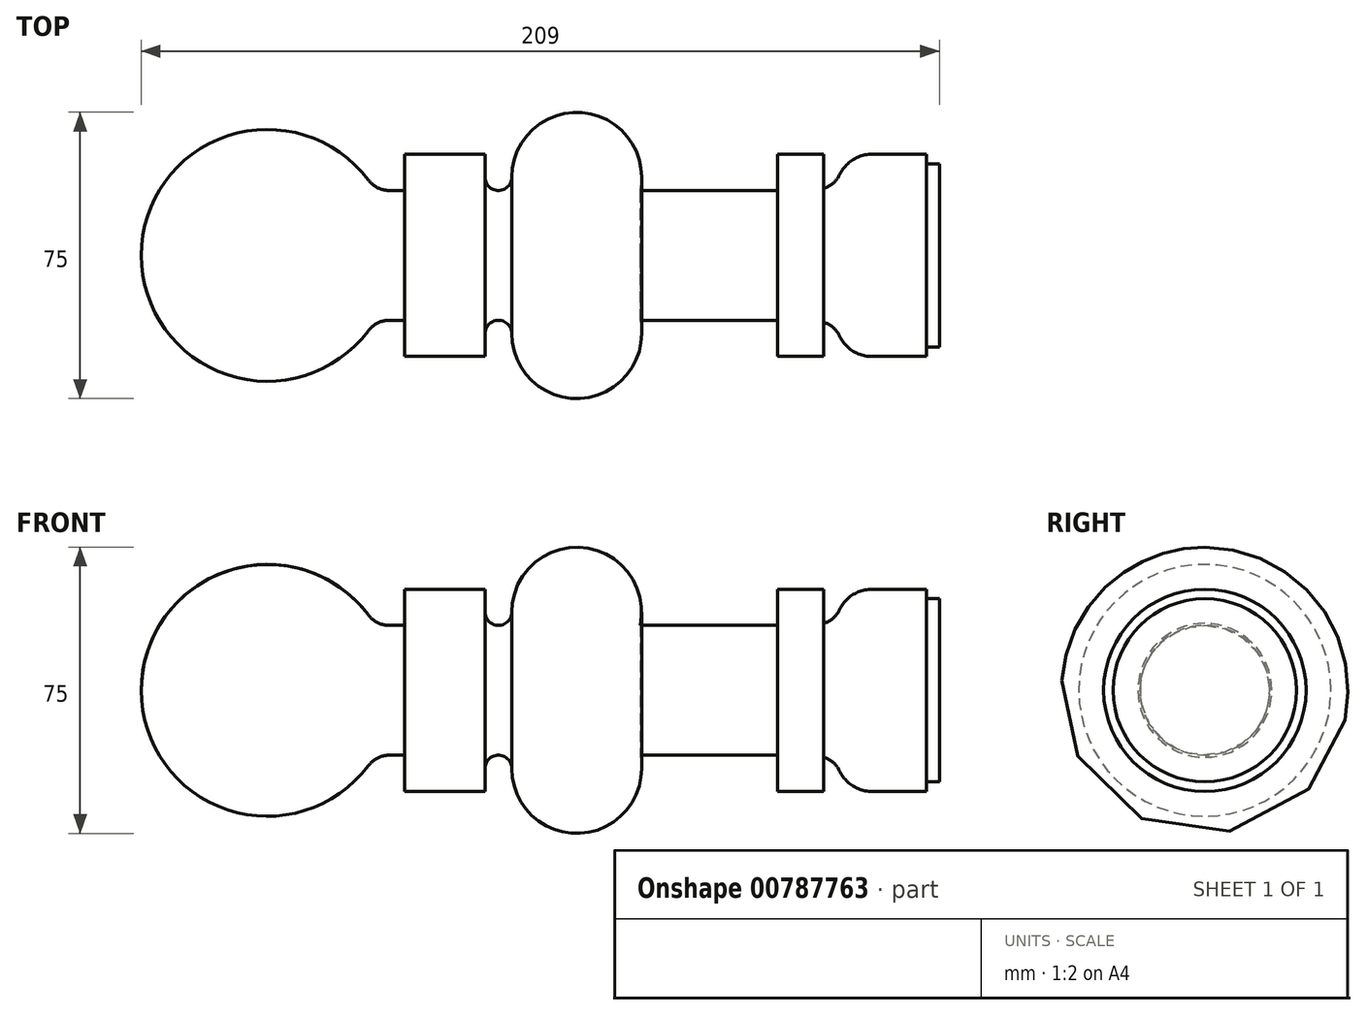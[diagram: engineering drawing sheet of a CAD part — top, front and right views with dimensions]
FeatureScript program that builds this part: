
annotation { "Feature Type Name" : "Feature", "Feature Type Description" : "" }
export const myFeature = defineFeature(function(context is Context, id is Id, definition is map)
    precondition{}
    {
        {
            var Q0;
            Q0=qCreatedBy(makeId("Front.planeOp"),FACE);
            var sketch = newSketch(context, id + "F0", { "sketchPlane" : qUnion([Q0])});
            skLineSegment(sketch, "E0", {"start": v(0, 0) * mm, "end": v(176, 0) * mm});
            skArc(sketch, "E1", {"start": v(26.4, 19.8) * mm, "mid": v(-10.44, 31.3) * mm, "end": v(-33, 0) * mm});
            skLineSegment(sketch, "E2", {"start": v(0, 0) * mm, "end": v(-33, 0) * mm});
            skLineSegment(sketch, "E3", {"start": v(36, 17) * mm, "end": v(36, 26.5) * mm});
            skLineSegment(sketch, "E4", {"start": v(36, 26.5) * mm, "end": v(57, 26.5) * mm});
            skLineSegment(sketch, "E5", {"start": v(57, 26.5) * mm, "end": v(57, 20.5) * mm});
            skLineSegment(sketch, "E6", {"start": v(36, 17) * mm, "end": v(32, 17) * mm});
            skArc(sketch, "E7.filletArc", {"start": v(26.4, 19.8) * mm, "mid": v(28.87, 17.74) * mm, "end": v(32, 17) * mm});
            skArc(sketch, "E8", {"start": v(57, 20.5) * mm, "mid": v(60.5, 17) * mm, "end": v(64, 20.5) * mm});
            skArc(sketch, "E9", {"start": v(97.64, 17) * mm, "mid": v(82.76, 37.4) * mm, "end": v(64, 20.5) * mm});
            skLineSegment(sketch, "E10", {"start": v(97.64, 17) * mm, "end": v(133.64, 17) * mm});
            skLineSegment(sketch, "E11", {"start": v(133.64, 17) * mm, "end": v(133.64, 26.5) * mm});
            skLineSegment(sketch, "E12", {"start": v(133.64, 26.5) * mm, "end": v(145.64, 26.5) * mm});
            skLineSegment(sketch, "E13", {"start": v(145.64, 26.5) * mm, "end": v(145.64, 17.54) * mm});
            skLineSegment(sketch, "E14", {"start": v(172.64, 24) * mm, "end": v(172.64, 26.5) * mm});
            skLineSegment(sketch, "E15", {"start": v(172.64, 26.5) * mm, "end": v(158.38, 26.5) * mm});
            skArc(sketch, "E16", {"start": v(158.38, 26.5) * mm, "mid": v(153.29, 25.02) * mm, "end": v(149.78, 21.04) * mm});
            skArc(sketch, "E17", {"start": v(145.64, 17.54) * mm, "mid": v(148.1, 18.84) * mm, "end": v(149.78, 21.04) * mm});
            skLineSegment(sketch, "E18", {"start": v(176, 0) * mm, "end": v(176, 24) * mm});
            skLineSegment(sketch, "E19", {"start": v(176, 24) * mm, "end": v(172.64, 24) * mm});
            skPoint(sketch, "E20.orphan", {"position": v(145.64, 0) * mm});
            skSolve(sketch);
        }
        {
            var Q0;
            Q0=makeQuery(id+"F0.imprint","IMPRINT",FACE,{"disambiguationData":[TD([[makeQuery(id+"F0.imprint","IMPRINT",EDGE,{"derivedFrom":sQuery(id+"F0.wireOp",EDGE,"E0")}),1.0]])]});
            var Q1;
            Q1=sQuery(id+"F0.wireOp",EDGE,"E0");
            revolve(context, id + "F1", {"surfaceOperationType" : NewSurfaceOperationType.NEW, "entities" : qUnion([Q0]), "axis" : qUnion([Q1]), "revolveType" : RevolveType.FULL});
        }
    });
